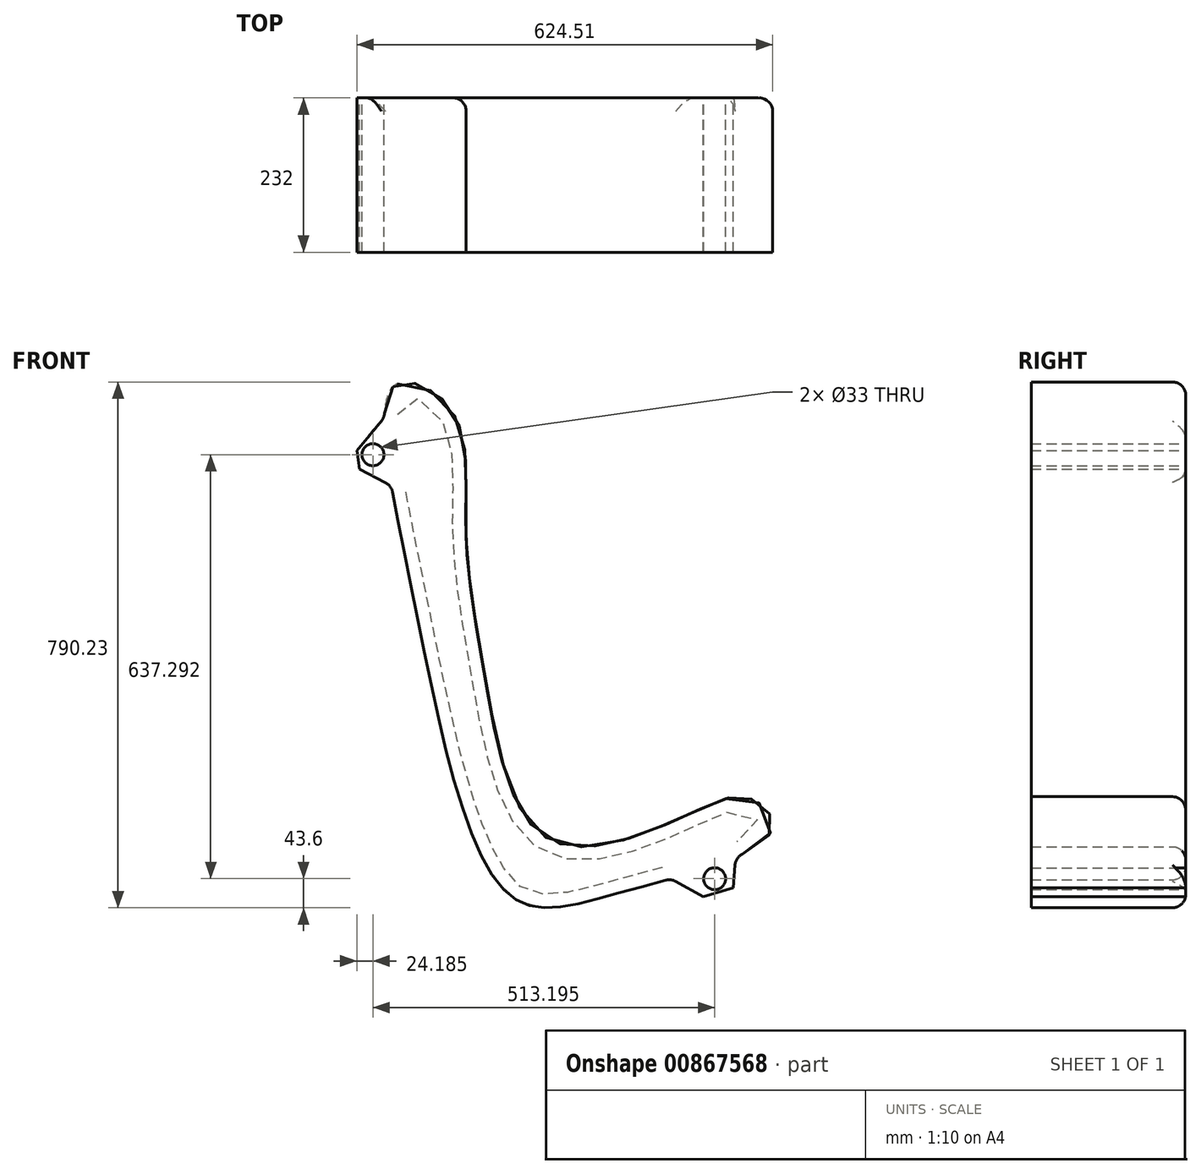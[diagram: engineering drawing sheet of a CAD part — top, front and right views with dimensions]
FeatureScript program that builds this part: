
annotation { "Feature Type Name" : "Feature", "Feature Type Description" : "" }
export const myFeature = defineFeature(function(context is Context, id is Id, definition is map)
    precondition{}
    {
        {
            var Q0;
            Q0=qCreatedBy(makeId("Front.planeOp"),FACE);
            var sketch = newSketch(context, id + "F0", { "sketchPlane" : qUnion([Q0])});
            skCircle(sketch, "E0", {"center": v(0, 0) * mm, "radius": 16.5 * mm});
            skCircle(sketch, "E1", {"center": v(-513.2, 637.3) * mm, "radius": 16.5 * mm});
            skFitSpline(sketch, "E2", {"points": [v(-478.55, 742.94) * mm, v(-394.54, 702.79) * mm, v(-374.05, 535.24) * mm, v(-344.9, 302.62) * mm, v(-247.07, 58.44) * mm, v(-40.47, 96.2) * mm, v(54.45, 120.3) * mm, v(85.72, 72.94) * mm, v(-140.85, -20.62) * mm, v(-310, -22.75) * mm, v(-456.44, 442.78) * mm, v(-478.55, 742.94) * mm]});
            skLineSegment(sketch, "E3", {"start": v(31.57, 32.59) * mm, "end": v(27.94, -13.64) * mm});
            skLineSegment(sketch, "E4", {"start": v(27.94, -13.64) * mm, "end": v(-17.1, -26.97) * mm});
            skLineSegment(sketch, "E5", {"start": v(-17.1, -26.97) * mm, "end": v(-65.72, 0) * mm});
            skLineSegment(sketch, "E6", {"start": v(-496.1, 693.19) * mm, "end": v(-537.38, 643.54) * mm});
            skLineSegment(sketch, "E7", {"start": v(-537.38, 643.54) * mm, "end": v(-533.61, 615.4) * mm});
            skLineSegment(sketch, "E8", {"start": v(-533.61, 615.4) * mm, "end": v(-485.5, 590.94) * mm});
            skSolve(sketch);
        }
        {
            var Q0;
            Q0=qSketchRegion(id+"F0",true);
            extrude(context, id + "F1", {"entities" : qUnion([Q0]), "depth" : 464 * mm, "offsetDistance" : 25 * mm});
        }
        {
            var Q0;
            {var subQ0=sQuery(id+"F0.wireOp",EDGE,"E2");Q0=makeQuery(id+"F1.opExtrude","SWEPT_FACE",FACE,{"disambiguationData":[OSD([subQ0]),TDD([makeQuery(id+"F0.imprint","IMPRINT",EDGE,{"disambiguationData":[TD([[makeQuery(id+"F0.imprint","INTERSECT",VERTEX,{"derivedFrom":[subQ0,sQuery(id+"F0.wireOp",EDGE,"E3")]}),1.0]])],"derivedFrom":subQ0})])]});}
            var Q1;
            {var subQ0=sQuery(id+"F0.wireOp",EDGE,"E2");Q1=makeQuery(id+"F1.opExtrude","SWEPT_FACE",FACE,{"disambiguationData":[OSD([subQ0]),TDD([makeQuery(id+"F0.imprint","IMPRINT",EDGE,{"disambiguationData":[TD([[makeQuery(id+"F0.imprint","INTERSECT",VERTEX,{"derivedFrom":[subQ0,sQuery(id+"F0.wireOp",EDGE,"E5")]}),-1.0]])],"derivedFrom":subQ0})])]});}
            fillet(context, id + "F2", {"entities" : qUnion([Q0, Q1]), "radius" : 20 * mm, "tangentPropagation" : true, "allowEdgeOverflow" : false});
        }
        {
            var Q0;
            Q0=makeQuery(id+"F2.opFillet","SPLIT",FACE,{"disambiguationData":[OD(0.0)],"derivedFrom":makeQuery(id+"F1.opExtrude","CAP_FACE",FACE,{"disambiguationData":[OSD([sQuery(id+"F0.wireOp",EDGE,"E0"),sQuery(id+"F0.wireOp",EDGE,"E1"),sQuery(id+"F0.wireOp",EDGE,"E2"),sQuery(id+"F0.wireOp",EDGE,"E3"),sQuery(id+"F0.wireOp",EDGE,"E4"),sQuery(id+"F0.wireOp",EDGE,"E5"),sQuery(id+"F0.wireOp",EDGE,"E6"),sQuery(id+"F0.wireOp",EDGE,"E7"),sQuery(id+"F0.wireOp",EDGE,"E8")])],"isStart":false})});
            var sketch = newSketch(context, id + "F3", { "sketchPlane" : qUnion([Q0])});
            skLineSegment(sketch, "E9.bottom", {"start": v(-765.68, 930.96) * mm, "end": v(278.14, 930.96) * mm});
            skLineSegment(sketch, "E9.top", {"start": v(-765.68, -214.37) * mm, "end": v(278.14, -214.37) * mm});
            skLineSegment(sketch, "E9.left", {"start": v(-765.68, 930.96) * mm, "end": v(-765.68, -214.37) * mm});
            skLineSegment(sketch, "E9.right", {"start": v(278.14, 930.96) * mm, "end": v(278.14, -214.37) * mm});
            skSolve(sketch);
        }
        {
            var Q0;
            Q0 = qSketchRegion(id + "F3", true);
            extrude(context, id + "F4", {"entities" : qUnion([Q0]), "operationType" : NewBodyOperationType.REMOVE, "oppositeDirection" : true, "depth" : 232 * mm, "offsetDistance" : 25 * mm});
        }
    });
